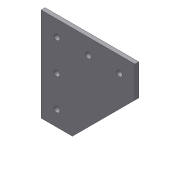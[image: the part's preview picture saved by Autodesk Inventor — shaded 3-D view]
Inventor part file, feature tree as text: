
AUTODESK INVENTOR PART (.ipt)
format: ipt  version: 2012 (Build 160160000, 160)  size: 88,576 bytes
history: native  units: in
note: dims shown in document units (in); Inventor stores cm internally (conversion verified against a paired STEP export)
features: extrude x2, pattern_linear x2, sketch x2
ambient origin geometry x8: Origin, YZ Plane, XZ Plane, XY Plane, X Axis, Y Axis, Z Axis, Center Point
bodies: Solid1 (feature_tree)
feature tree (6):
  extrude  "Extrusion1"  Depth=3.0in
  extrude  "Extrusion2"  Depth=1.0in
  pattern_linear  "Rectangular Pattern1"  Spacing1=0.125in  [1 undecoded]
  pattern_linear  "Rectangular Pattern2"  Spacing1=0.1875in  [1 undecoded]
  sketch  "Sketch1"  dims[d0=3.0in d1=3.0in]
  sketch  "Sketch2"  dims[d2=1.0in d3=1.0in d4=0.125in d5=0.0in d6=0.1875in d7=0.5in d8=0.5in d9=0.125in d10=0.0in d11=1.5748in d13=1.0in d14=1.5748in d16=1.0in]
note: 2 required parameter values undecoded (feature->parameter linkage not recoverable at this tier; creation-order binding heuristic only, values carry confidence <= 0.55)
